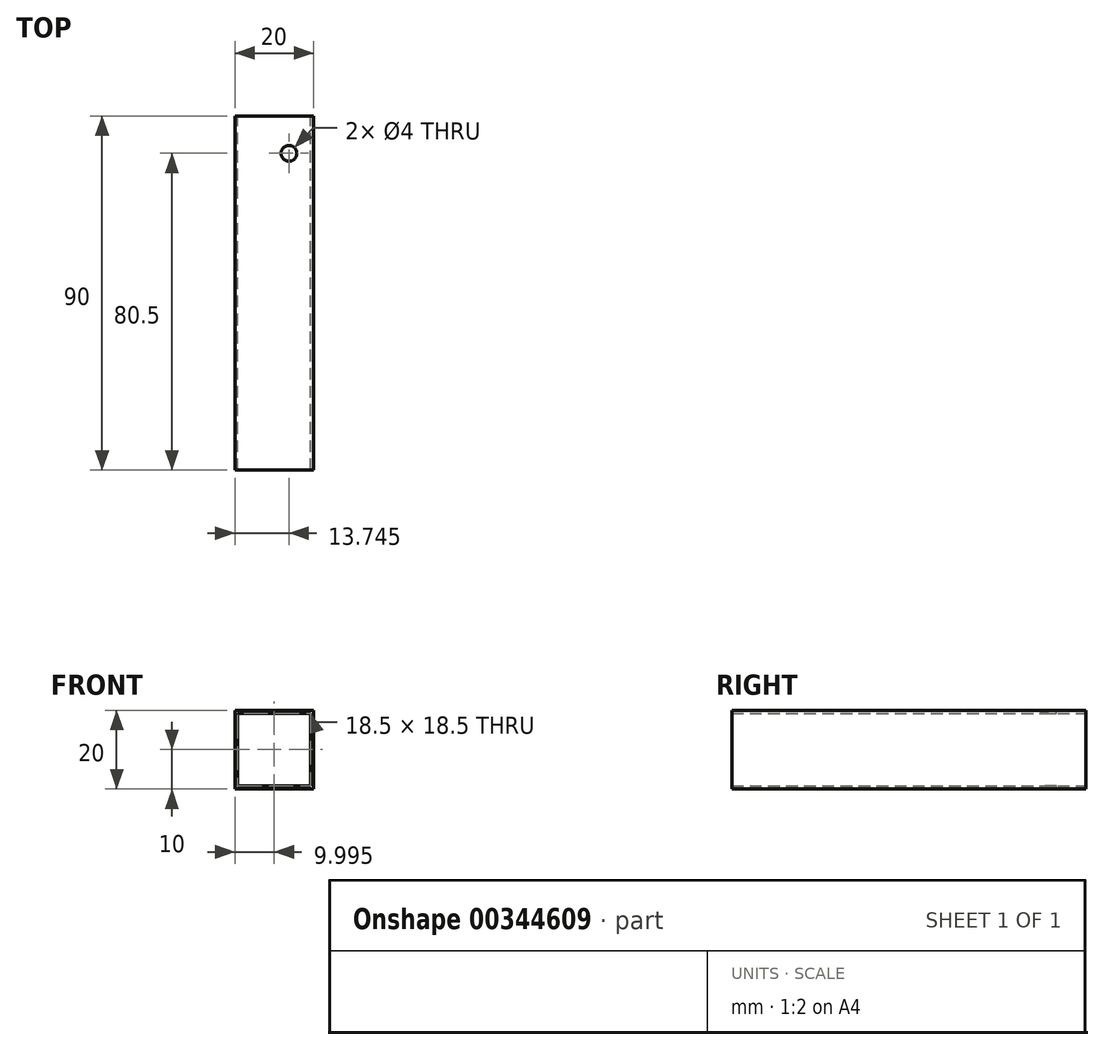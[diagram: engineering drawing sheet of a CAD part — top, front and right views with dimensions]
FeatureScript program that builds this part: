
annotation { "Feature Type Name" : "Feature", "Feature Type Description" : "" }
export const myFeature = defineFeature(function(context is Context, id is Id, definition is map)
    precondition{}
    {
        {
            var Q0;
            Q0=qCreatedBy(makeId("Front.planeOp"),FACE);
            var sketch = newSketch(context, id + "F0", { "sketchPlane" : qUnion([Q0])});
            skLineSegment(sketch, "E0.bottom", {"start": v(-34.48, 27) * mm, "end": v(-54.48, 27) * mm});
            skLineSegment(sketch, "E0.top", {"start": v(-34.48, 47) * mm, "end": v(-54.48, 47) * mm});
            skLineSegment(sketch, "E0.left", {"start": v(-34.48, 27) * mm, "end": v(-34.48, 47) * mm});
            skLineSegment(sketch, "E0.right", {"start": v(-54.48, 27) * mm, "end": v(-54.48, 47) * mm});
            skPoint(sketch, "E0.middle", {"position": v(-44.48, 37) * mm});
            skLineSegment(sketch, "E1.bottom", {"start": v(-35.23, 27.75) * mm, "end": v(-53.73, 27.75) * mm});
            skLineSegment(sketch, "E1.top", {"start": v(-35.23, 46.25) * mm, "end": v(-53.73, 46.25) * mm});
            skLineSegment(sketch, "E1.left", {"start": v(-35.23, 27.75) * mm, "end": v(-35.23, 46.25) * mm});
            skLineSegment(sketch, "E1.right", {"start": v(-53.73, 27.75) * mm, "end": v(-53.73, 46.25) * mm});
            skSolve(sketch);
        }
        {
            var Q0;
            Q0=makeQuery(id+"F0.imprint","IMPRINT",FACE,{"disambiguationData":[TD([[makeQuery(id+"F0.imprint","IMPRINT",EDGE,{"derivedFrom":sQuery(id+"F0.wireOp",EDGE,"E0.bottom")}),-1.0]])]});
            extrude(context, id + "F1", {"entities" : qUnion([Q0]), "depth" : 90 * mm});
        }
        {
            var Q0;
            Q0=makeQuery(id+"F1.opExtrude","SWEPT_FACE",FACE,{"disambiguationData":[OSD([sQuery(id+"F0.wireOp",EDGE,"E0.top")])]});
            var sketch = newSketch(context, id + "F2", { "sketchPlane" : qUnion([Q0])});
            skLineSegment(sketch, "E2", {"start": v(-54.48, 0) * mm, "end": v(-40.73, 0) * mm});
            skLineSegment(sketch, "E3", {"start": v(-40.73, 0) * mm, "end": v(-40.73, -9.5) * mm});
            skCircle(sketch, "E4", {"center": v(-40.73, -9.5) * mm, "radius": 2 * mm});
            skSolve(sketch);
        }
        {
            var Q0;
            Q0 = qSketchRegion(id + "F2", true);
            extrude(context, id + "F3", {"entities" : qUnion([Q0]), "operationType" : NewBodyOperationType.REMOVE, "oppositeDirection" : true, "depth" : 25 * mm});
        }
    });
